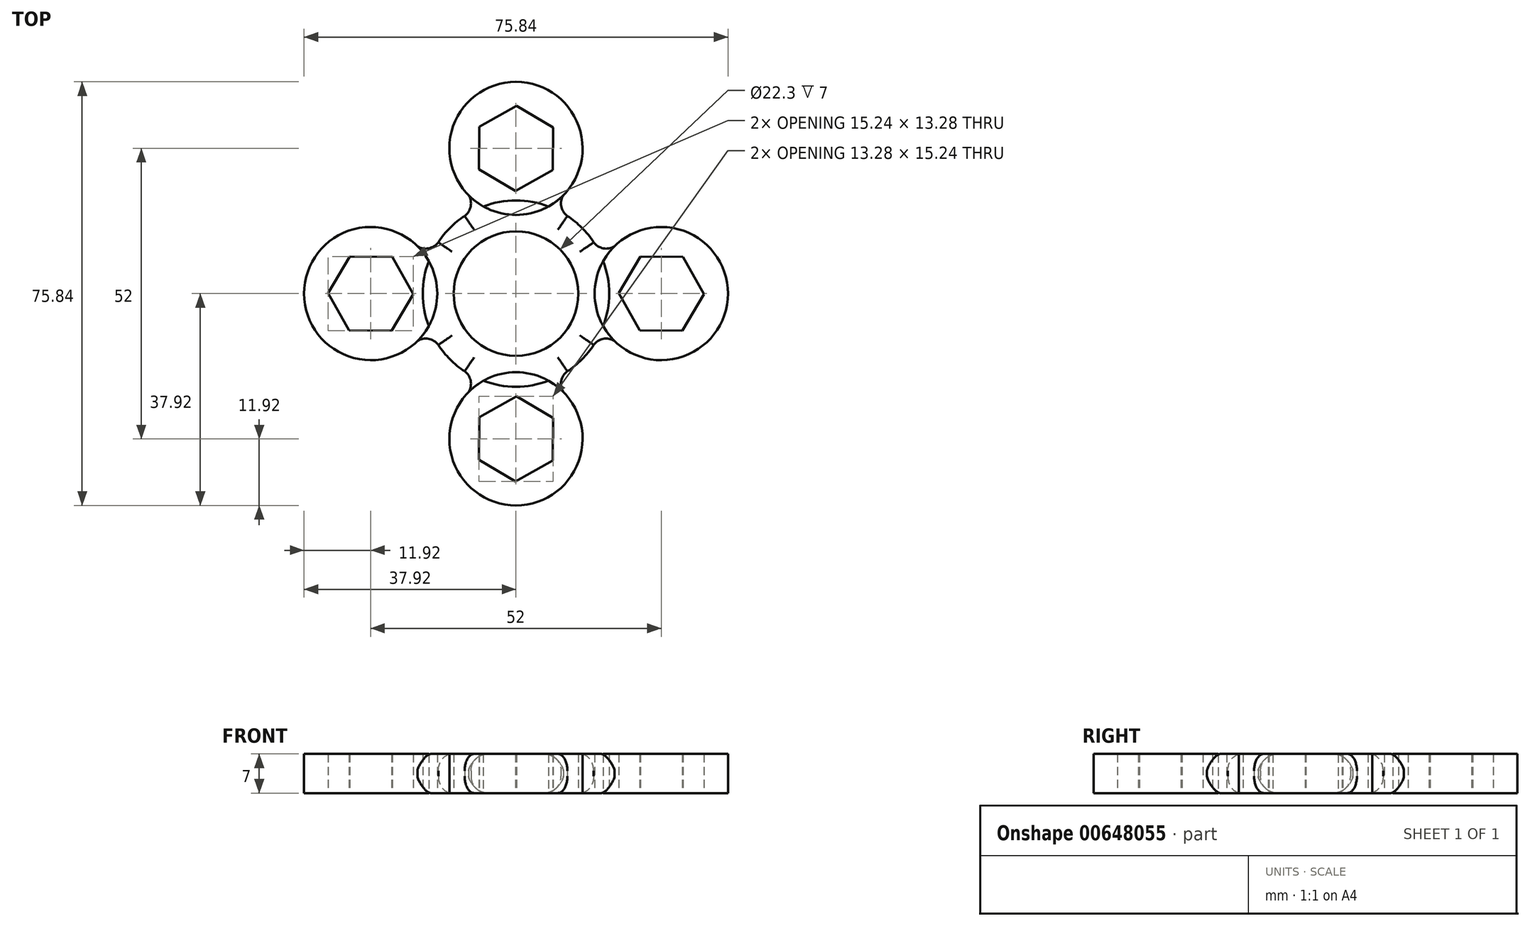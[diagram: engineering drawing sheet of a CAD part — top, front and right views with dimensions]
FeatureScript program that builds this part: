
annotation { "Feature Type Name" : "Feature", "Feature Type Description" : "" }
export const myFeature = defineFeature(function(context is Context, id is Id, definition is map)
    precondition{}
    {
        {
            var Q0;
            Q0=qCreatedBy(makeId("Top.planeOp"),FACE);
            var sketch = newSketch(context, id + "F0", { "sketchPlane" : qUnion([Q0])});
            skCircle(sketch, "E0", {"center": v(0, 0) * mm, "radius": 11.15 * mm});
            skCircle(sketch, "E1.cCircle", {"center": v(26, 0) * mm, "radius": 6.6 * mm, "construction": true});
            skLineSegment(sketch, "E1.0", {"start": v(29.88, 6.56) * mm, "end": v(33.62, -0.09) * mm});
            skLineSegment(sketch, "E1.1", {"start": v(33.62, -0.09) * mm, "end": v(29.74, -6.64) * mm});
            skLineSegment(sketch, "E1.2", {"start": v(29.74, -6.64) * mm, "end": v(22.12, -6.56) * mm});
            skLineSegment(sketch, "E1.3", {"start": v(22.12, -6.56) * mm, "end": v(18.38, 0.09) * mm});
            skLineSegment(sketch, "E1.4", {"start": v(18.38, 0.09) * mm, "end": v(22.26, 6.64) * mm});
            skLineSegment(sketch, "E1.5", {"start": v(22.26, 6.64) * mm, "end": v(29.88, 6.56) * mm});
            skPoint(sketch, "E1.0.midPoint", {"position": v(31.75, 3.24) * mm});
            skCircle(sketch, "E2", {"center": v(26, 0) * mm, "radius": 11.92 * mm});
            skArc(sketch, "E3", {"start": v(18.38, -9.16) * mm, "mid": v(16.01, -8.06) * mm, "end": v(13.77, -9.4) * mm});
            skArc(sketch, "E4.MirrorCS", {"start": v(18.38, 9.16) * mm, "mid": v(16.01, 8.06) * mm, "end": v(13.77, 9.4) * mm});
            skCircle(sketch, "E5.MirrorC", {"center": v(0, 0) * mm, "radius": 16.67 * mm});
            skArc(sketch, "E6.1.0", {"start": v(-9.16, 18.38) * mm, "mid": v(-8.06, 16.01) * mm, "end": v(-9.4, 13.77) * mm});
            skLineSegment(sketch, "E6.1.1", {"start": v(6.64, 29.74) * mm, "end": v(6.56, 22.12) * mm});
            skLineSegment(sketch, "E6.1.2", {"start": v(-6.56, 29.88) * mm, "end": v(0.09, 33.62) * mm});
            skLineSegment(sketch, "E6.1.3", {"start": v(-6.64, 22.26) * mm, "end": v(-6.56, 29.88) * mm});
            skArc(sketch, "E6.1.4", {"start": v(9.16, 18.38) * mm, "mid": v(8.06, 16.01) * mm, "end": v(9.4, 13.77) * mm});
            skCircle(sketch, "E6.1.5", {"center": v(0, 26) * mm, "radius": 11.92 * mm});
            skLineSegment(sketch, "E6.1.6", {"start": v(-0.09, 18.38) * mm, "end": v(-6.64, 22.26) * mm});
            skPoint(sketch, "E6.1.7", {"position": v(-3.24, 31.75) * mm});
            skLineSegment(sketch, "E6.1.8", {"start": v(0.09, 33.62) * mm, "end": v(6.64, 29.74) * mm});
            skLineSegment(sketch, "E6.1.9", {"start": v(6.56, 22.12) * mm, "end": v(-0.09, 18.38) * mm});
            skCircle(sketch, "E6.1.10", {"center": v(0, 26) * mm, "radius": 6.6 * mm, "construction": true});
            skCircle(sketch, "E6.1.11", {"center": v(0, 26) * mm, "radius": 11.92 * mm});
            skArc(sketch, "E6.2.0", {"start": v(-18.38, -9.16) * mm, "mid": v(-16.01, -8.06) * mm, "end": v(-13.77, -9.4) * mm});
            skLineSegment(sketch, "E6.2.1", {"start": v(-29.74, 6.64) * mm, "end": v(-22.12, 6.56) * mm});
            skLineSegment(sketch, "E6.2.2", {"start": v(-29.88, -6.56) * mm, "end": v(-33.62, 0.09) * mm});
            skLineSegment(sketch, "E6.2.3", {"start": v(-22.26, -6.64) * mm, "end": v(-29.88, -6.56) * mm});
            skArc(sketch, "E6.2.4", {"start": v(-18.38, 9.16) * mm, "mid": v(-16.01, 8.06) * mm, "end": v(-13.77, 9.4) * mm});
            skCircle(sketch, "E6.2.5", {"center": v(-26, 0) * mm, "radius": 11.92 * mm});
            skLineSegment(sketch, "E6.2.6", {"start": v(-18.38, -0.09) * mm, "end": v(-22.26, -6.64) * mm});
            skPoint(sketch, "E6.2.7", {"position": v(-31.75, -3.24) * mm});
            skLineSegment(sketch, "E6.2.8", {"start": v(-33.62, 0.09) * mm, "end": v(-29.74, 6.64) * mm});
            skLineSegment(sketch, "E6.2.9", {"start": v(-22.12, 6.56) * mm, "end": v(-18.38, -0.09) * mm});
            skCircle(sketch, "E6.2.10", {"center": v(-26, 0) * mm, "radius": 6.6 * mm, "construction": true});
            skCircle(sketch, "E6.2.11", {"center": v(-26, 0) * mm, "radius": 11.92 * mm});
            skArc(sketch, "E6.3.0", {"start": v(9.16, -18.38) * mm, "mid": v(8.06, -16.01) * mm, "end": v(9.4, -13.77) * mm});
            skLineSegment(sketch, "E6.3.1", {"start": v(-6.64, -29.74) * mm, "end": v(-6.56, -22.12) * mm});
            skLineSegment(sketch, "E6.3.2", {"start": v(6.56, -29.88) * mm, "end": v(-0.09, -33.62) * mm});
            skLineSegment(sketch, "E6.3.3", {"start": v(6.64, -22.26) * mm, "end": v(6.56, -29.88) * mm});
            skArc(sketch, "E6.3.4", {"start": v(-9.16, -18.38) * mm, "mid": v(-8.06, -16.01) * mm, "end": v(-9.4, -13.77) * mm});
            skCircle(sketch, "E6.3.5", {"center": v(0, -26) * mm, "radius": 11.92 * mm});
            skLineSegment(sketch, "E6.3.6", {"start": v(0.09, -18.38) * mm, "end": v(6.64, -22.26) * mm});
            skPoint(sketch, "E6.3.7", {"position": v(3.24, -31.75) * mm});
            skLineSegment(sketch, "E6.3.8", {"start": v(-0.09, -33.62) * mm, "end": v(-6.64, -29.74) * mm});
            skLineSegment(sketch, "E6.3.9", {"start": v(-6.56, -22.12) * mm, "end": v(0.09, -18.38) * mm});
            skCircle(sketch, "E6.3.10", {"center": v(0, -26) * mm, "radius": 6.6 * mm, "construction": true});
            skCircle(sketch, "E6.3.11", {"center": v(0, -26) * mm, "radius": 11.92 * mm});
            skSolve(sketch);
        }
        {
            var Q0;
            Q0 = qSketchRegion(id + "F0", true);
            extrude(context, id + "F1", {"entities" : qUnion([Q0]), "depth" : 7 * mm, "offsetDistance" : 25 * mm});
        }
        {
            var Q0;
            {var subQ0=sQuery(id+"F0.wireOp",EDGE,"E6.2.11");var subQ1=sQuery(id+"F0.wireOp",EDGE,"E6.2.0");var subQ2=makeQuery(id+"F0.imprint","INTERSECT",VERTEX,{"disambiguationData":[OD(0.0)],"derivedFrom":[subQ1,subQ0]});var subQ3=sQuery(id+"F0.wireOp",EDGE,"E6.2.4");var subQ4=makeQuery(id+"F0.imprint","INTERSECT",VERTEX,{"disambiguationData":[OD(0.0)],"derivedFrom":[subQ3,subQ0]});Q0=makeQuery(id+"F1.opExtrude","CAP_EDGE",EDGE,{"disambiguationData":[OSD([subQ0]),TDD([makeQuery(id+"F0.imprint","IMPRINT",EDGE,{"disambiguationData":[TD([[subQ2,-1.0]])],"derivedFrom":subQ0}),makeQuery(id+"F0.imprint","IMPRINT",EDGE,{"disambiguationData":[TD([[subQ4,1.0]])],"derivedFrom":subQ0}),makeQuery(id+"F0.imprint","IMPRINT",EDGE,{"disambiguationData":[TD([[subQ2,1.0]])],"derivedFrom":subQ0})])],"isStart":false});}
            var Q1;
            Q1=makeQuery(id+"F1.opExtrude","CAP_EDGE",EDGE,{"disambiguationData":[OSD([sQuery(id+"F0.wireOp",EDGE,"E6.2.4")])],"isStart":false});
            var Q2;
            {var subQ0=sQuery(id+"F0.wireOp",EDGE,"E6.1.0");var subQ1=sQuery(id+"F0.wireOp",EDGE,"E5.MirrorC");var subQ2=makeQuery(id+"F0.imprint","INTERSECT",VERTEX,{"disambiguationData":[OD(0.0)],"derivedFrom":[subQ1,subQ0]});var subQ3=sQuery(id+"F0.wireOp",EDGE,"E6.2.4");var subQ4=makeQuery(id+"F0.imprint","INTERSECT",VERTEX,{"disambiguationData":[OD(0.0)],"derivedFrom":[subQ1,subQ3]});Q2=makeQuery(id+"F1.opExtrude","CAP_EDGE",EDGE,{"disambiguationData":[OSD([subQ1]),TDD([makeQuery(id+"F0.imprint","IMPRINT",EDGE,{"disambiguationData":[TD([[subQ4,1.0]])],"derivedFrom":subQ1}),makeQuery(id+"F0.imprint","IMPRINT",EDGE,{"disambiguationData":[TD([[subQ2,1.0]])],"derivedFrom":subQ1}),makeQuery(id+"F0.imprint","IMPRINT",EDGE,{"disambiguationData":[TD([[subQ2,-1.0]])],"derivedFrom":subQ1})])],"isStart":false});}
            var Q3;
            Q3=makeQuery(id+"F1.opExtrude","CAP_EDGE",EDGE,{"disambiguationData":[OSD([sQuery(id+"F0.wireOp",EDGE,"E6.1.0")])],"isStart":false});
            var Q4;
            {var subQ0=sQuery(id+"F0.wireOp",EDGE,"E6.1.11");var subQ1=sQuery(id+"F0.wireOp",EDGE,"E6.1.0");var subQ2=makeQuery(id+"F0.imprint","INTERSECT",VERTEX,{"disambiguationData":[OD(0.0)],"derivedFrom":[subQ1,subQ0]});var subQ3=sQuery(id+"F0.wireOp",EDGE,"E6.1.4");var subQ4=makeQuery(id+"F0.imprint","INTERSECT",VERTEX,{"disambiguationData":[OD(0.0)],"derivedFrom":[subQ3,subQ0]});Q4=makeQuery(id+"F1.opExtrude","CAP_EDGE",EDGE,{"disambiguationData":[OSD([subQ0]),TDD([makeQuery(id+"F0.imprint","IMPRINT",EDGE,{"disambiguationData":[TD([[subQ2,-1.0]])],"derivedFrom":subQ0}),makeQuery(id+"F0.imprint","IMPRINT",EDGE,{"disambiguationData":[TD([[subQ4,1.0]])],"derivedFrom":subQ0}),makeQuery(id+"F0.imprint","IMPRINT",EDGE,{"disambiguationData":[TD([[subQ2,1.0]])],"derivedFrom":subQ0})])],"isStart":false});}
            var Q5;
            Q5=makeQuery(id+"F1.opExtrude","CAP_EDGE",EDGE,{"disambiguationData":[OSD([sQuery(id+"F0.wireOp",EDGE,"E6.1.4")])],"isStart":false});
            var Q6;
            {var subQ0=sQuery(id+"F0.wireOp",EDGE,"E5.MirrorC");var subQ1=sQuery(id+"F0.wireOp",EDGE,"E4.MirrorCS");var subQ2=makeQuery(id+"F0.imprint","INTERSECT",VERTEX,{"disambiguationData":[OD(0.0)],"derivedFrom":[subQ1,subQ0]});var subQ3=sQuery(id+"F0.wireOp",EDGE,"E6.1.4");var subQ4=makeQuery(id+"F0.imprint","INTERSECT",VERTEX,{"disambiguationData":[OD(0.0)],"derivedFrom":[subQ0,subQ3]});Q6=makeQuery(id+"F1.opExtrude","CAP_EDGE",EDGE,{"disambiguationData":[OSD([subQ0]),TDD([makeQuery(id+"F0.imprint","IMPRINT",EDGE,{"disambiguationData":[TD([[subQ4,1.0]])],"derivedFrom":subQ0}),makeQuery(id+"F0.imprint","IMPRINT",EDGE,{"disambiguationData":[TD([[subQ2,1.0]])],"derivedFrom":subQ0}),makeQuery(id+"F0.imprint","IMPRINT",EDGE,{"disambiguationData":[TD([[subQ2,-1.0]])],"derivedFrom":subQ0})])],"isStart":false});}
            var Q7;
            Q7=makeQuery(id+"F1.opExtrude","CAP_EDGE",EDGE,{"disambiguationData":[OSD([sQuery(id+"F0.wireOp",EDGE,"E4.MirrorCS")])],"isStart":false});
            var Q8;
            {var subQ0=sQuery(id+"F0.wireOp",EDGE,"E6.2.11");var subQ1=sQuery(id+"F0.wireOp",EDGE,"E6.2.0");var subQ2=makeQuery(id+"F0.imprint","INTERSECT",VERTEX,{"disambiguationData":[OD(0.0)],"derivedFrom":[subQ1,subQ0]});var subQ3=sQuery(id+"F0.wireOp",EDGE,"E6.2.4");var subQ4=makeQuery(id+"F0.imprint","INTERSECT",VERTEX,{"disambiguationData":[OD(0.0)],"derivedFrom":[subQ3,subQ0]});Q8=makeQuery(id+"F1.opExtrude","CAP_EDGE",EDGE,{"disambiguationData":[OSD([subQ0]),TDD([makeQuery(id+"F0.imprint","IMPRINT",EDGE,{"disambiguationData":[TD([[subQ2,-1.0]])],"derivedFrom":subQ0}),makeQuery(id+"F0.imprint","IMPRINT",EDGE,{"disambiguationData":[TD([[subQ4,1.0]])],"derivedFrom":subQ0}),makeQuery(id+"F0.imprint","IMPRINT",EDGE,{"disambiguationData":[TD([[subQ2,1.0]])],"derivedFrom":subQ0})])],"isStart":true});}
            var Q9;
            Q9=makeQuery(id+"F1.opExtrude","CAP_EDGE",EDGE,{"disambiguationData":[OSD([sQuery(id+"F0.wireOp",EDGE,"E6.2.0")])],"isStart":true});
            var Q10;
            {var subQ0=sQuery(id+"F0.wireOp",EDGE,"E6.2.0");var subQ1=sQuery(id+"F0.wireOp",EDGE,"E5.MirrorC");var subQ2=makeQuery(id+"F0.imprint","INTERSECT",VERTEX,{"disambiguationData":[OD(0.0)],"derivedFrom":[subQ1,subQ0]});var subQ3=sQuery(id+"F0.wireOp",EDGE,"E6.3.4");var subQ4=makeQuery(id+"F0.imprint","INTERSECT",VERTEX,{"disambiguationData":[OD(0.0)],"derivedFrom":[subQ1,subQ3]});Q10=makeQuery(id+"F1.opExtrude","CAP_EDGE",EDGE,{"disambiguationData":[OSD([subQ1]),TDD([makeQuery(id+"F0.imprint","IMPRINT",EDGE,{"disambiguationData":[TD([[subQ4,1.0]])],"derivedFrom":subQ1}),makeQuery(id+"F0.imprint","IMPRINT",EDGE,{"disambiguationData":[TD([[subQ2,1.0]])],"derivedFrom":subQ1}),makeQuery(id+"F0.imprint","IMPRINT",EDGE,{"disambiguationData":[TD([[subQ2,-1.0]])],"derivedFrom":subQ1})])],"isStart":true});}
            var Q11;
            Q11=makeQuery(id+"F1.opExtrude","CAP_EDGE",EDGE,{"disambiguationData":[OSD([sQuery(id+"F0.wireOp",EDGE,"E6.3.4")])],"isStart":true});
            var Q12;
            {var subQ0=sQuery(id+"F0.wireOp",EDGE,"E6.3.11");var subQ1=sQuery(id+"F0.wireOp",EDGE,"E6.3.0");var subQ2=makeQuery(id+"F0.imprint","INTERSECT",VERTEX,{"disambiguationData":[OD(0.0)],"derivedFrom":[subQ1,subQ0]});var subQ3=sQuery(id+"F0.wireOp",EDGE,"E6.3.4");var subQ4=makeQuery(id+"F0.imprint","INTERSECT",VERTEX,{"disambiguationData":[OD(0.0)],"derivedFrom":[subQ3,subQ0]});Q12=makeQuery(id+"F1.opExtrude","CAP_EDGE",EDGE,{"disambiguationData":[OSD([subQ0]),TDD([makeQuery(id+"F0.imprint","IMPRINT",EDGE,{"disambiguationData":[TD([[subQ2,-1.0]])],"derivedFrom":subQ0}),makeQuery(id+"F0.imprint","IMPRINT",EDGE,{"disambiguationData":[TD([[subQ4,1.0]])],"derivedFrom":subQ0}),makeQuery(id+"F0.imprint","IMPRINT",EDGE,{"disambiguationData":[TD([[subQ2,1.0]])],"derivedFrom":subQ0})])],"isStart":true});}
            var Q13;
            Q13=makeQuery(id+"F1.opExtrude","CAP_EDGE",EDGE,{"disambiguationData":[OSD([sQuery(id+"F0.wireOp",EDGE,"E6.3.0")])],"isStart":true});
            var Q14;
            {var subQ0=sQuery(id+"F0.wireOp",EDGE,"E6.3.0");var subQ1=sQuery(id+"F0.wireOp",EDGE,"E5.MirrorC");var subQ2=makeQuery(id+"F0.imprint","INTERSECT",VERTEX,{"disambiguationData":[OD(0.0)],"derivedFrom":[subQ1,subQ0]});var subQ3=sQuery(id+"F0.wireOp",EDGE,"E3");var subQ4=makeQuery(id+"F0.imprint","INTERSECT",VERTEX,{"disambiguationData":[OD(0.0)],"derivedFrom":[subQ3,subQ1]});Q14=makeQuery(id+"F1.opExtrude","CAP_EDGE",EDGE,{"disambiguationData":[OSD([subQ1]),TDD([makeQuery(id+"F0.imprint","IMPRINT",EDGE,{"disambiguationData":[TD([[subQ4,1.0]])],"derivedFrom":subQ1}),makeQuery(id+"F0.imprint","IMPRINT",EDGE,{"disambiguationData":[TD([[subQ4,-1.0]])],"derivedFrom":subQ1}),makeQuery(id+"F0.imprint","IMPRINT",EDGE,{"disambiguationData":[TD([[subQ2,-1.0]])],"derivedFrom":subQ1})])],"isStart":true});}
            var Q15;
            Q15=makeQuery(id+"F1.opExtrude","CAP_EDGE",EDGE,{"disambiguationData":[OSD([sQuery(id+"F0.wireOp",EDGE,"E3")])],"isStart":true});
            var Q16;
            {var subQ0=sQuery(id+"F0.wireOp",EDGE,"E2");var subQ1=sQuery(id+"F0.wireOp",EDGE,"E3");var subQ2=makeQuery(id+"F0.imprint","INTERSECT",VERTEX,{"disambiguationData":[OD(0.0)],"derivedFrom":[subQ1,subQ0]});var subQ3=sQuery(id+"F0.wireOp",EDGE,"E4.MirrorCS");var subQ4=makeQuery(id+"F0.imprint","INTERSECT",VERTEX,{"disambiguationData":[OD(0.0)],"derivedFrom":[subQ3,subQ0]});Q16=makeQuery(id+"F1.opExtrude","CAP_EDGE",EDGE,{"disambiguationData":[OSD([subQ0]),TDD([makeQuery(id+"F0.imprint","IMPRINT",EDGE,{"disambiguationData":[TD([[subQ2,-1.0]])],"derivedFrom":subQ0}),makeQuery(id+"F0.imprint","IMPRINT",EDGE,{"disambiguationData":[TD([[subQ4,1.0]])],"derivedFrom":subQ0}),makeQuery(id+"F0.imprint","IMPRINT",EDGE,{"disambiguationData":[TD([[subQ2,1.0]])],"derivedFrom":subQ0})])],"isStart":true});}
            var Q17;
            Q17=makeQuery(id+"F1.opExtrude","CAP_EDGE",EDGE,{"disambiguationData":[OSD([sQuery(id+"F0.wireOp",EDGE,"E4.MirrorCS")])],"isStart":true});
            var Q18;
            {var subQ0=sQuery(id+"F0.wireOp",EDGE,"E5.MirrorC");var subQ1=sQuery(id+"F0.wireOp",EDGE,"E4.MirrorCS");var subQ2=makeQuery(id+"F0.imprint","INTERSECT",VERTEX,{"disambiguationData":[OD(0.0)],"derivedFrom":[subQ1,subQ0]});var subQ3=sQuery(id+"F0.wireOp",EDGE,"E6.1.4");var subQ4=makeQuery(id+"F0.imprint","INTERSECT",VERTEX,{"disambiguationData":[OD(0.0)],"derivedFrom":[subQ0,subQ3]});Q18=makeQuery(id+"F1.opExtrude","CAP_EDGE",EDGE,{"disambiguationData":[OSD([subQ0]),TDD([makeQuery(id+"F0.imprint","IMPRINT",EDGE,{"disambiguationData":[TD([[subQ4,1.0]])],"derivedFrom":subQ0}),makeQuery(id+"F0.imprint","IMPRINT",EDGE,{"disambiguationData":[TD([[subQ2,1.0]])],"derivedFrom":subQ0}),makeQuery(id+"F0.imprint","IMPRINT",EDGE,{"disambiguationData":[TD([[subQ2,-1.0]])],"derivedFrom":subQ0})])],"isStart":true});}
            var Q19;
            Q19=makeQuery(id+"F1.opExtrude","CAP_EDGE",EDGE,{"disambiguationData":[OSD([sQuery(id+"F0.wireOp",EDGE,"E6.1.4")])],"isStart":true});
            var Q20;
            {var subQ0=sQuery(id+"F0.wireOp",EDGE,"E6.1.11");var subQ1=sQuery(id+"F0.wireOp",EDGE,"E6.1.0");var subQ2=makeQuery(id+"F0.imprint","INTERSECT",VERTEX,{"disambiguationData":[OD(0.0)],"derivedFrom":[subQ1,subQ0]});var subQ3=sQuery(id+"F0.wireOp",EDGE,"E6.1.4");var subQ4=makeQuery(id+"F0.imprint","INTERSECT",VERTEX,{"disambiguationData":[OD(0.0)],"derivedFrom":[subQ3,subQ0]});Q20=makeQuery(id+"F1.opExtrude","CAP_EDGE",EDGE,{"disambiguationData":[OSD([subQ0]),TDD([makeQuery(id+"F0.imprint","IMPRINT",EDGE,{"disambiguationData":[TD([[subQ2,-1.0]])],"derivedFrom":subQ0}),makeQuery(id+"F0.imprint","IMPRINT",EDGE,{"disambiguationData":[TD([[subQ4,1.0]])],"derivedFrom":subQ0}),makeQuery(id+"F0.imprint","IMPRINT",EDGE,{"disambiguationData":[TD([[subQ2,1.0]])],"derivedFrom":subQ0})])],"isStart":true});}
            var Q21;
            Q21=makeQuery(id+"F1.opExtrude","CAP_EDGE",EDGE,{"disambiguationData":[OSD([sQuery(id+"F0.wireOp",EDGE,"E6.1.0")])],"isStart":true});
            var Q22;
            {var subQ0=sQuery(id+"F0.wireOp",EDGE,"E6.1.0");var subQ1=sQuery(id+"F0.wireOp",EDGE,"E5.MirrorC");var subQ2=makeQuery(id+"F0.imprint","INTERSECT",VERTEX,{"disambiguationData":[OD(0.0)],"derivedFrom":[subQ1,subQ0]});var subQ3=sQuery(id+"F0.wireOp",EDGE,"E6.2.4");var subQ4=makeQuery(id+"F0.imprint","INTERSECT",VERTEX,{"disambiguationData":[OD(0.0)],"derivedFrom":[subQ1,subQ3]});Q22=makeQuery(id+"F1.opExtrude","CAP_EDGE",EDGE,{"disambiguationData":[OSD([subQ1]),TDD([makeQuery(id+"F0.imprint","IMPRINT",EDGE,{"disambiguationData":[TD([[subQ4,1.0]])],"derivedFrom":subQ1}),makeQuery(id+"F0.imprint","IMPRINT",EDGE,{"disambiguationData":[TD([[subQ2,1.0]])],"derivedFrom":subQ1}),makeQuery(id+"F0.imprint","IMPRINT",EDGE,{"disambiguationData":[TD([[subQ2,-1.0]])],"derivedFrom":subQ1})])],"isStart":true});}
            var Q23;
            Q23=makeQuery(id+"F1.opExtrude","CAP_EDGE",EDGE,{"disambiguationData":[OSD([sQuery(id+"F0.wireOp",EDGE,"E6.2.4")])],"isStart":true});
            var Q24;
            Q24=makeQuery(id+"F1.opExtrude","CAP_EDGE",EDGE,{"disambiguationData":[OSD([sQuery(id+"F0.wireOp",EDGE,"E6.2.0")])],"isStart":false});
            var Q25;
            {var subQ0=sQuery(id+"F0.wireOp",EDGE,"E6.2.0");var subQ1=sQuery(id+"F0.wireOp",EDGE,"E5.MirrorC");var subQ2=makeQuery(id+"F0.imprint","INTERSECT",VERTEX,{"disambiguationData":[OD(0.0)],"derivedFrom":[subQ1,subQ0]});var subQ3=sQuery(id+"F0.wireOp",EDGE,"E6.3.4");var subQ4=makeQuery(id+"F0.imprint","INTERSECT",VERTEX,{"disambiguationData":[OD(0.0)],"derivedFrom":[subQ1,subQ3]});Q25=makeQuery(id+"F1.opExtrude","CAP_EDGE",EDGE,{"disambiguationData":[OSD([subQ1]),TDD([makeQuery(id+"F0.imprint","IMPRINT",EDGE,{"disambiguationData":[TD([[subQ4,1.0]])],"derivedFrom":subQ1}),makeQuery(id+"F0.imprint","IMPRINT",EDGE,{"disambiguationData":[TD([[subQ2,1.0]])],"derivedFrom":subQ1}),makeQuery(id+"F0.imprint","IMPRINT",EDGE,{"disambiguationData":[TD([[subQ2,-1.0]])],"derivedFrom":subQ1})])],"isStart":false});}
            var Q26;
            Q26=makeQuery(id+"F1.opExtrude","CAP_EDGE",EDGE,{"disambiguationData":[OSD([sQuery(id+"F0.wireOp",EDGE,"E6.3.4")])],"isStart":false});
            var Q27;
            {var subQ0=sQuery(id+"F0.wireOp",EDGE,"E6.3.11");var subQ1=sQuery(id+"F0.wireOp",EDGE,"E6.3.0");var subQ2=makeQuery(id+"F0.imprint","INTERSECT",VERTEX,{"disambiguationData":[OD(0.0)],"derivedFrom":[subQ1,subQ0]});var subQ3=sQuery(id+"F0.wireOp",EDGE,"E6.3.4");var subQ4=makeQuery(id+"F0.imprint","INTERSECT",VERTEX,{"disambiguationData":[OD(0.0)],"derivedFrom":[subQ3,subQ0]});Q27=makeQuery(id+"F1.opExtrude","CAP_EDGE",EDGE,{"disambiguationData":[OSD([subQ0]),TDD([makeQuery(id+"F0.imprint","IMPRINT",EDGE,{"disambiguationData":[TD([[subQ2,-1.0]])],"derivedFrom":subQ0}),makeQuery(id+"F0.imprint","IMPRINT",EDGE,{"disambiguationData":[TD([[subQ4,1.0]])],"derivedFrom":subQ0}),makeQuery(id+"F0.imprint","IMPRINT",EDGE,{"disambiguationData":[TD([[subQ2,1.0]])],"derivedFrom":subQ0})])],"isStart":false});}
            var Q28;
            {var subQ0=sQuery(id+"F0.wireOp",EDGE,"E2");var subQ1=sQuery(id+"F0.wireOp",EDGE,"E3");var subQ2=makeQuery(id+"F0.imprint","INTERSECT",VERTEX,{"disambiguationData":[OD(0.0)],"derivedFrom":[subQ1,subQ0]});var subQ3=sQuery(id+"F0.wireOp",EDGE,"E4.MirrorCS");var subQ4=makeQuery(id+"F0.imprint","INTERSECT",VERTEX,{"disambiguationData":[OD(0.0)],"derivedFrom":[subQ3,subQ0]});Q28=makeQuery(id+"F1.opExtrude","CAP_EDGE",EDGE,{"disambiguationData":[OSD([subQ0]),TDD([makeQuery(id+"F0.imprint","IMPRINT",EDGE,{"disambiguationData":[TD([[subQ2,-1.0]])],"derivedFrom":subQ0}),makeQuery(id+"F0.imprint","IMPRINT",EDGE,{"disambiguationData":[TD([[subQ4,1.0]])],"derivedFrom":subQ0}),makeQuery(id+"F0.imprint","IMPRINT",EDGE,{"disambiguationData":[TD([[subQ2,1.0]])],"derivedFrom":subQ0})])],"isStart":false});}
            var Q29;
            Q29=makeQuery(id+"F1.opExtrude","CAP_EDGE",EDGE,{"disambiguationData":[OSD([sQuery(id+"F0.wireOp",EDGE,"E3")])],"isStart":false});
            var Q30;
            {var subQ0=sQuery(id+"F0.wireOp",EDGE,"E6.3.0");var subQ1=sQuery(id+"F0.wireOp",EDGE,"E5.MirrorC");var subQ2=makeQuery(id+"F0.imprint","INTERSECT",VERTEX,{"disambiguationData":[OD(0.0)],"derivedFrom":[subQ1,subQ0]});var subQ3=sQuery(id+"F0.wireOp",EDGE,"E3");var subQ4=makeQuery(id+"F0.imprint","INTERSECT",VERTEX,{"disambiguationData":[OD(0.0)],"derivedFrom":[subQ3,subQ1]});Q30=makeQuery(id+"F1.opExtrude","CAP_EDGE",EDGE,{"disambiguationData":[OSD([subQ1]),TDD([makeQuery(id+"F0.imprint","IMPRINT",EDGE,{"disambiguationData":[TD([[subQ4,1.0]])],"derivedFrom":subQ1}),makeQuery(id+"F0.imprint","IMPRINT",EDGE,{"disambiguationData":[TD([[subQ4,-1.0]])],"derivedFrom":subQ1}),makeQuery(id+"F0.imprint","IMPRINT",EDGE,{"disambiguationData":[TD([[subQ2,-1.0]])],"derivedFrom":subQ1})])],"isStart":false});}
            var Q31;
            Q31=makeQuery(id+"F1.opExtrude","CAP_EDGE",EDGE,{"disambiguationData":[OSD([sQuery(id+"F0.wireOp",EDGE,"E6.3.0")])],"isStart":false});
            fillet(context, id + "F2", {"entities" : qUnion([Q0, Q1, Q2, Q3, Q4, Q5, Q6, Q7, Q8, Q9, Q10, Q11, Q12, Q13, Q14, Q15, Q16, Q17, Q18, Q19, Q20, Q21, Q22, Q23, Q24, Q25, Q26, Q27, Q28, Q29, Q30, Q31]), "radius" : 3 * mm, "tangentPropagation" : true, "allowEdgeOverflow" : false});
        }
    });
